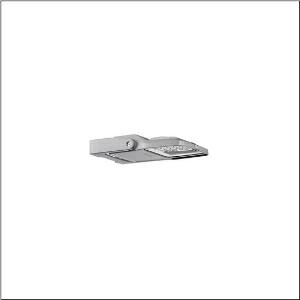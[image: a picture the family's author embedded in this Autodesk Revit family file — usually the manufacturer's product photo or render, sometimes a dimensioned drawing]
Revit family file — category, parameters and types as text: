
# Revit family: floodlight_fl_21_iq_micro___pl33t_5xa7762a2f2a_46b5
name_source: partatom
category: Lighting Fixtures
units: mm (PartAtom-declared; Revit-internal decimal feet)

## family parameters
Cut with Voids When Loaded = No
Host = Face
Light Source = No
Part Type = Normal
Room Calculation Point = No
Round Connector Dimension = Use Diameter
Shared = No

## types (1)
- --- (1 x LED, 2930 lm, 23.1 W, 3000K)
    Apparent Load = 23 VA
    CIE Flux Codes = 26 75 99 100 100
    Color Rendering = 70
    Color Temperature = 3000K
    Default Elevation = 1800 mm
    Description = Floodlight FL 21 iQ micro, floodlight, primary light control with lens, of PMMA, primary optical cover: protective disc, of toughened safety glass, transparent, light distribution: PL33T, light emission: direct distribution, installation type: surface-mounted, LED, High Power LED, rated luminous flux: 2.930lm, luminous efficacy: 127lm/W, light colour: 730, colour temperature: 3000K, control: Auto-Match, Temp-Guard, Night-Set, Smart-Wire, Desk-Remote (wireless, voltage-free reading and setting of iQ features in the workshop via application-optimized NFC function/RFID function), optimised constant luminous flux control (CLO 2.0), Street-Remote, with terminal, 6-pole, mains connection: 220..240V, AC, 50/60Hz, start of lifetime: 23W, end of service life: 24W, reduction: 11W, luminaire housing, of diecast aluminium, powder-coated, Siteco® metallic grey (DB 702S), corrosivity category C5 mid according to DIN EN ISO 12944, sealing non-destructively replaceable, design bracket, of diecast aluminium, powder-coated, Siteco® metallic grey (DB 702S), protection rating (complete): IP66, insulation class (complete): insulation class II (safety insulation), certification: CE, ENEC, VDE, protection symbol: D, impact resistance: IK07, permissible operating ambient temperature: -40..+40°C, permissible operating ambient temperature for outdoor applications: -40..+50°C, standard: DIN EN 12944, LABS conformity tested according to VDMA 24364:2018-05, packaging unit: 1 piece

Light Distribution: PL33T
    Height = 65 mm
    Lamp = 1 x LED
    Lamp Light Flux = 2930 lm
    Lamp Power = 23.1 W
    Lamp count = 1
    Length = 312 mm
    Luminous efficacy = 127 lm/W
    Manufacturer = Siteco
    ModVariant = No
    Model = 5XA7762A2F2A
    Mounting Place = Wall
    Mounting Type = Surface mounted
    Number of Poles = 1
    OnlyDefault = Yes
    Power Factor = 1
    Product Name = Floodlight FL 21 iQ micro | PL33T
    Product group = floodlight | wall mounted
    ProductGroupID = 2001
    Protection Class = Protection class II
    Protection Degree = IP 66
    RLX_Detail_Level = 1
    RLX_Emergency_Light_Flux = 0 lm
    RLX_Emergency_Type = 0
    RLX_Emergency_Type_DB = No
    RlxData = <blob elided: 97133 chars, md5=95694cdc>
    Socket = socket
    Standby Power = 0 W
    System Light Flux = 2930 lm
    System Power = 23 W
    Type Comments = factory setting: luminous flux: 100 % | dim-lin: 254 | 455 mA
    Type Image = l_1006878.jpg
    URL = http://relux.com
    VarID = @adj_080493
    Voltage = 0 V
    Weight = 0.00 kg
    Width = 230 mm

## geometry (parser evidence)
native form markers: Blend x4, Sweep x11
no freeform markers — native parametric forms only
